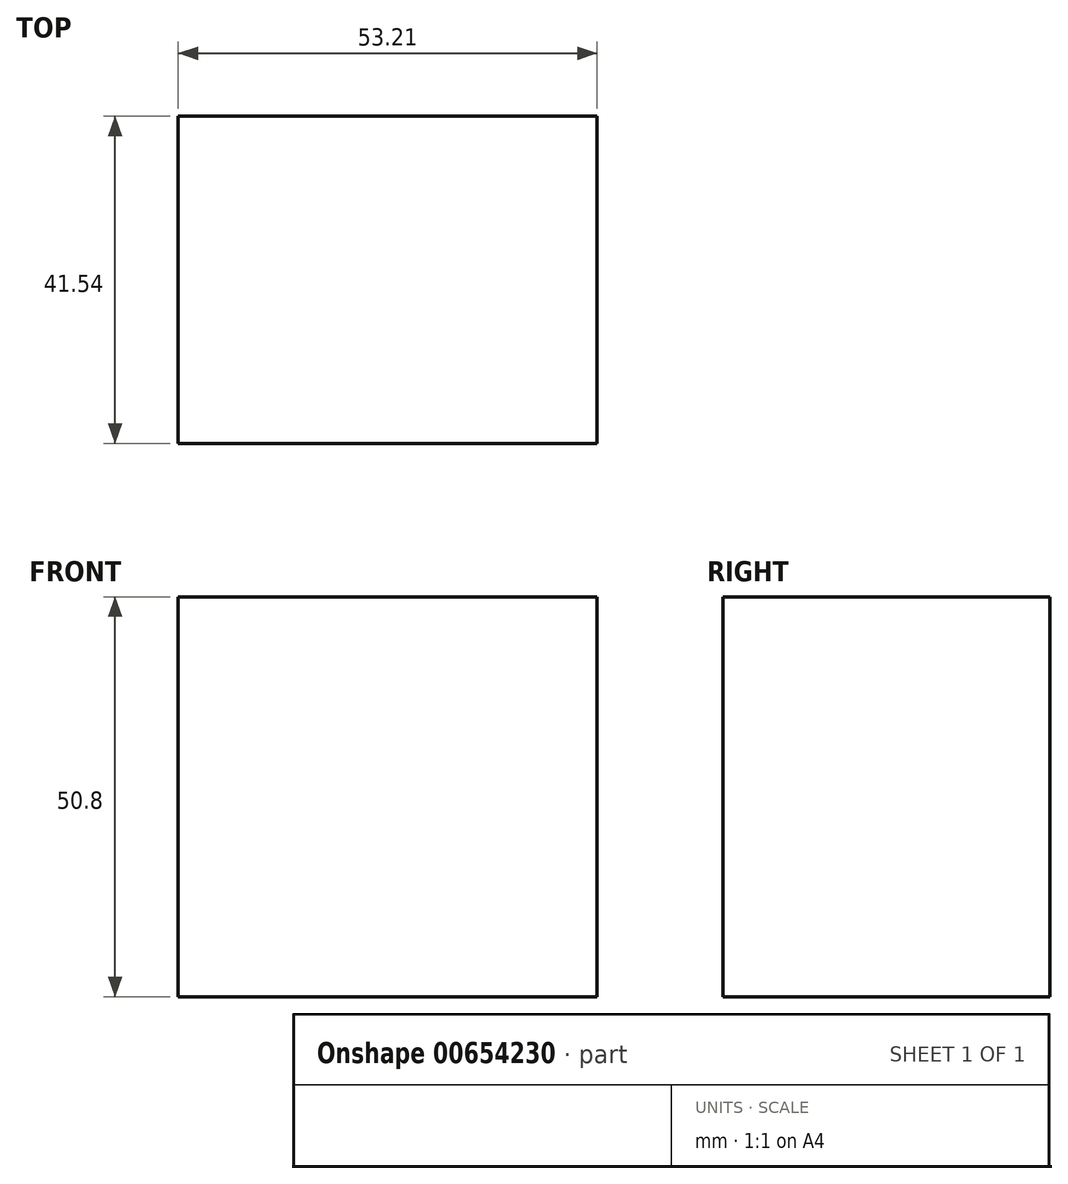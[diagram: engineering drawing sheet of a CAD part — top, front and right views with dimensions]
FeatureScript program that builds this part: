
annotation { "Feature Type Name" : "Feature", "Feature Type Description" : "" }
export const myFeature = defineFeature(function(context is Context, id is Id, definition is map)
    precondition{}
    {
        {
            var Q0;
            Q0=qCreatedBy(makeId("Top.planeOp"),FACE);
            var sketch = newSketch(context, id + "F0", { "sketchPlane" : qUnion([Q0])});
            skLineSegment(sketch, "E0.bottom", {"start": v(0, 0) * mm, "end": v(53.21, 0) * mm});
            skLineSegment(sketch, "E0.top", {"start": v(0, 41.54) * mm, "end": v(53.21, 41.54) * mm});
            skLineSegment(sketch, "E0.left", {"start": v(0, 0) * mm, "end": v(0, 41.54) * mm});
            skLineSegment(sketch, "E0.right", {"start": v(53.21, 0) * mm, "end": v(53.21, 41.54) * mm});
            skSolve(sketch);
        }
        {
            var Q0;
            Q0=makeQuery(id+"F0.imprint","IMPRINT",FACE,{"disambiguationData":[TD([[makeQuery(id+"F0.imprint","IMPRINT",EDGE,{"derivedFrom":sQuery(id+"F0.wireOp",EDGE,"E0.bottom")}),1.0]])]});
            extrude(context, id + "F1", {"entities" : qUnion([Q0]), "depth" : 50.8 * mm, "offsetDistance" : 25.4 * mm});
        }
    });
